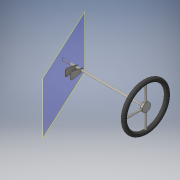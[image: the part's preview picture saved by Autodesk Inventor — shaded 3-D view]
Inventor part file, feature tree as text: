
AUTODESK INVENTOR PART (.ipt)
format: ipt  version: 2016 (Build 200138000, 138)  size: 377,856 bytes
history: native  units: in
note: dims shown in document units (in); Inventor stores cm internally (conversion verified against a paired STEP export)
features: sketch x8, extrude x7, other x3, hole x2, fillet x2, plane x1, pattern_circular x1, mirror x1
ambient origin geometry x8: Origin, YZ Plane, XZ Plane, XY Plane, X Axis, Y Axis, Z Axis, Center Point
bodies: Solid1 (feature_tree)
feature tree (25):
  extrude  "Rod"  Depth=16.0in TaperAngle=0.0deg
  extrude  "Plate1"  Depth=0.325in
  plane  "Work Plane1"
  extrude  "Plate2"  Depth=0.125in TaperAngle=0.0deg
  hole  "Connecting Threads1"  [1 undecoded]
  hole  "Connecting Threads2"  [1 undecoded]
  other  "Steering Wheel"
  extrude  "Steering Wheel Spoke"  Depth=1.0in
  pattern_circular  "Steering Wheel Spokes"  [2 undecoded]
  fillet  "Welds"  Radius=5.0in
  extrude  "Steering Wheel Center Hub"  Depth=3.0in TaperAngle=180.0deg
  fillet  "Welds2"  Radius=2.0in
  mirror  "Mirror1"
  extrude  "Fix"  Depth=3.0in TaperAngle=0.0deg
  other  "Plate Midplane"
  extrude  "Rod1"  Depth=0.125in
  other  "Floor plane"
  sketch  "Sketch1"  dims[d0=0.5in d1=16.0in d2=0.0in]
  sketch  "Sketch2"  dims[d3=0.75in d6=0.325in]
  sketch  "Sketch3"  dims[d7=1.0625in d8=0.125in d9=0.0in]
  sketch  "Sketch5"  dims[d10=1.25in d11=0.125in d12=0.0in]
  sketch  "Sketch7"  dims[d33=1.0in d34=1.0in d15=0.211in d16=0.5in d17=0.375in d18=0.25in d19=0.5635in d20=0.679in d21=0.8108in]
  sketch  "Sketch8"  dims[d31=1.0in d32=1.0in d24=0.196in d25=0.5in d26=0.375in d27=0.25in d28=0.5635in d29=1.0in d30=0.8108in d35=0.125in]
  sketch  "Sketch10"  dims[d37=5.0in d38=1.0in]
  sketch  "Sketch11"  dims[d39=90.0deg d41=0.5in d42=5.0in d43=0.0in d44=1.1811in d45=180.0deg d47=2.0in d48=0.5in d49=0.0in d50=0.125in d51=2.25in d52=1.0in d53=0.0in d54=0.5in d55=3.0in d56=0.0in d57=1.0651in]
note: 4 required parameter values undecoded (feature->parameter linkage not recoverable at this tier; creation-order binding heuristic only, values carry confidence <= 0.55)
